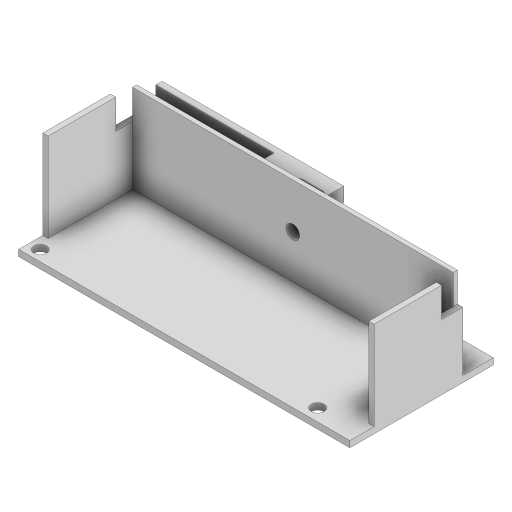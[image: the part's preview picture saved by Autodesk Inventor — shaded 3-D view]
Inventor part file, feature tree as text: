
AUTODESK INVENTOR PART (.ipt)
format: ipt  version: 2023.3 (Build 273359000, 359)  size: 329,216 bytes
history: native  units: mm
features: extrude x13, sketch x12, projected_geometry x3, fillet x1, chamfer x1, loft x1, mirror x1, plane x1
ambient origin geometry x8: Origin, YZ Plane, XZ Plane, XY Plane, X Axis, Y Axis, Z Axis, Center Point
bodies: Solid1 (feature_tree)
feature tree (33):
  extrude  "Extrusion1"  Depth=22.5mm
  sketch  "Sketch2"  dims[d2=1.5mm d3=33.0mm d4=0.0mm]
  extrude  "Extrusion2"  Depth=1.5mm TaperAngle=0.0deg
  extrude  "Extrusion3"  Depth=4.25mm
  extrude  "Extrusion4"  Depth=1.5mm
  extrude  "Extrusion5"  Depth=1.5mm
  sketch  "Sketch4"  dims[d7=1.5mm d8=1.5mm]
  extrude  "Extrusion6"  Depth=1.0mm
  extrude  "Extrusion7"  Depth=7.65mm
  fillet  "Fillet1"  Radius=2.65mm
  extrude  "Extrusion8"  Depth=17.5mm TaperAngle=0.0deg
  chamfer  "Chamfer1"  Distance=21.0mm
  extrude  "Extrusion9"  Depth=17.5mm
  loft  "Loft1"
  extrude  "Extrusion10"  Depth=5.5mm
  mirror  "Mirror1"
  extrude  "Extrusion11"  Depth=3.0mm
  plane  "Work Plane1"
  extrude  "Extrusion12"  Depth=10.0mm TaperAngle=0.0deg
  extrude  "Extrusion13"  Depth=3.0mm
  sketch  "Sketch13"  dims[d32=10.0mm d33=0.0mm d34=3.15mm d35=10.0mm d36=0.0mm d37=10.35mm d38=2.0mm d43=5.0mm d44=11.85mm d45=39.25mm d46=3.0mm d47=0.0mm d49=3.0mm d50=2.0mm d51=45.0deg d52=1.0mm d53=21.0mm d54=0.0mm d55=4.0mm d56=3.0mm d57=5.0mm d58=5.0mm d59=3.0mm d60=2.0mm d61=0.0mm d62=90.0deg d63=0.0mm d64=90.0deg d65=7.0mm d66=5.0mm d67=0.0mm d68=5.0mm d69=0.0mm d73=135.0deg d74=45.0deg d75=3.0mm d76=0.5mm d77=3.0mm d78=0.0mm d79=3.0mm d80=2.5mm d81=2.62mm d82=3.0mm d83=2.875mm d84=10.5mm d85=3.0mm d86=0.0mm]
  sketch  "Sketch1"  dims[d0=22.5mm d1=78.5mm]
  sketch  "Sketch3"  dims[d5=28.0mm d6=4.25mm]
  projected_geometry  "Projected Loop1"
  sketch  "Sketch6"  dims[d9=1.5mm d10=20.0mm]
  sketch  "Sketch7"  dims[d11=76.0mm d12=1.0mm]
  sketch  "Sketch8"  dims[d13=4.65mm d14=7.65mm d16=2.65mm]
  sketch  "Sketch9"  dims[d17=5.65mm d18=17.5mm d19=0.0mm d20=21.0mm d21=0.0mm]
  sketch  "Sketch10"  dims[d22=17.5mm d23=0.0mm d24=75.7mm]
  sketch  "Sketch11"  dims[d25=20.7mm d28=3.15mm]
  projected_geometry  "Projected Loop2"
  sketch  "Sketch12"  dims[d29=7.0mm d30=0.0mm d31=5.5mm]
  projected_geometry  "Projected Loop3"
